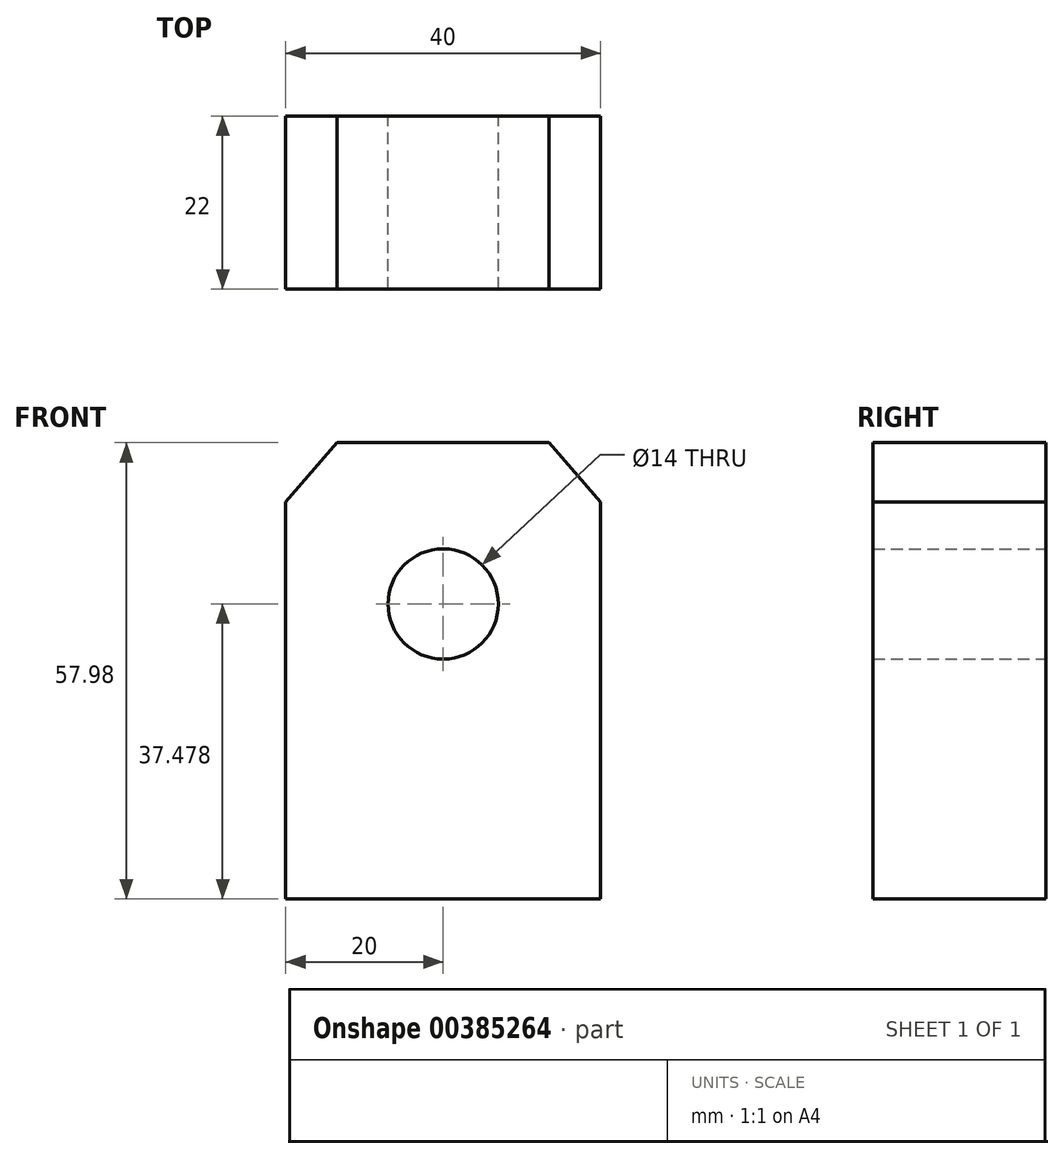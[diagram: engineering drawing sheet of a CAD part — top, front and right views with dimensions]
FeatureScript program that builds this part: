
annotation { "Feature Type Name" : "Feature", "Feature Type Description" : "" }
export const myFeature = defineFeature(function(context is Context, id is Id, definition is map)
    precondition{}
    {
        {
            var Q0;
            Q0=qCreatedBy(makeId("Front.planeOp"),FACE);
            var sketch = newSketch(context, id + "F0", { "sketchPlane" : qUnion([Q0])});
            skLineSegment(sketch, "E0.top", {"start": v(-20, -25.2) * mm, "end": v(20, -25.2) * mm});
            skLineSegment(sketch, "E0.left", {"start": v(-20, 25.2) * mm, "end": v(-20, -25.2) * mm});
            skLineSegment(sketch, "E0.right", {"start": v(20, 25.2) * mm, "end": v(20, -25.2) * mm});
            skPoint(sketch, "E0.middle", {"position": v(0, 0) * mm});
            skLineSegment(sketch, "E1", {"start": v(-20, 25.2) * mm, "end": v(-13.47, 32.78) * mm});
            skLineSegment(sketch, "E2", {"start": v(-13.47, 32.78) * mm, "end": v(13.47, 32.78) * mm});
            skLineSegment(sketch, "E3", {"start": v(13.47, 32.78) * mm, "end": v(20, 25.2) * mm});
            skCircle(sketch, "E4", {"center": v(0, 12.28) * mm, "radius": 7 * mm});
            skSolve(sketch);
        }
        {
            var Q0;
            Q0 = qSketchRegion(id + "F0", true);
            extrude(context, id + "F1", {"entities" : qUnion([Q0]), "depth" : 22 * mm});
        }
    });
